# Revit family: Sink-Vanity_Top-Lavatory-KOHLER-Reve-K-5026K_1
name_source: partatom
category: Plumbing Fixtures
revit_build: Autodesk Revit 2017 (Build: 20160225_1515(x64)
units: mm (PartAtom-declared; Revit-internal decimal feet)

## family parameters
Cut with Voids When Loaded = No
Host = Face
OmniClass Number = 23.31.13.00
OmniClass Title = Sinks
Part Type = Normal
Room Calculation Point = No
Round Connector Dimension = Use Diameter
Shared = No

## types (4) — shared parameters
ADA Compliant = No
Assembly Code = D2010400
CW Connection = No
Cold Water Inlet = Cold Water Inlet
Date Modified = 08/19/2020
Default Elevation = 36"
Drain Included = No
HW Connection = No
Height = 7 1/2"
Hot Water Inlet = Hot Water Inlet
Length = 39 3/8"
Manufacturer = KOHLER Co.
MasterFormat 2014 = 22 41 16
MasterFormat 2014 Name = Residential Lavatories and Sinks
Material = Fireclay
Product Name = Reve
URL = https://www.kohlerasiapacific.com
Vent Connection = No
Waste Connection = Yes
Waste Water Outlet = Waste Water Outlet
WaterSense Certified = No
Width = 18 5/16"

## per-type parameters (varying)
| type | Description | Faucet Hole Distance | Finish | Model | Type | Widespread Faucet Hole |
| Single Faucet Hole,0-White | Vanity Lavatory with Single faucet holes | 0" | Kohler-Fireclay-0-White | K-5026K-1-0 | 1 | No |
| Single Faucet Hole,HW1-Honed White | Vanity Lavatory with Single faucet holes | 0" | KOHLER-Fireclay-HW1-Honed_White | K-5026K-1-HW1 | 2 | No |
| 8 Inch Widespread Faucet Hole,0-White | Vanity Lavatory with 8 inch widespread faucet holes | 8 1/16" | Kohler-Fireclay-0-White | K-5026K-8-0 | 3 | Yes |
| 8 Inch Widespread Faucet Hole,HW1-Honed White | Vanity Lavatory with 8 inch widespread faucet holes | 8 1/16" | KOHLER-Fireclay-HW1-Honed_White | K-5026K-8-HW1 | 4 | Yes |

## geometry (parser evidence)
native form markers: Sweep x6
no freeform markers — native parametric forms only
